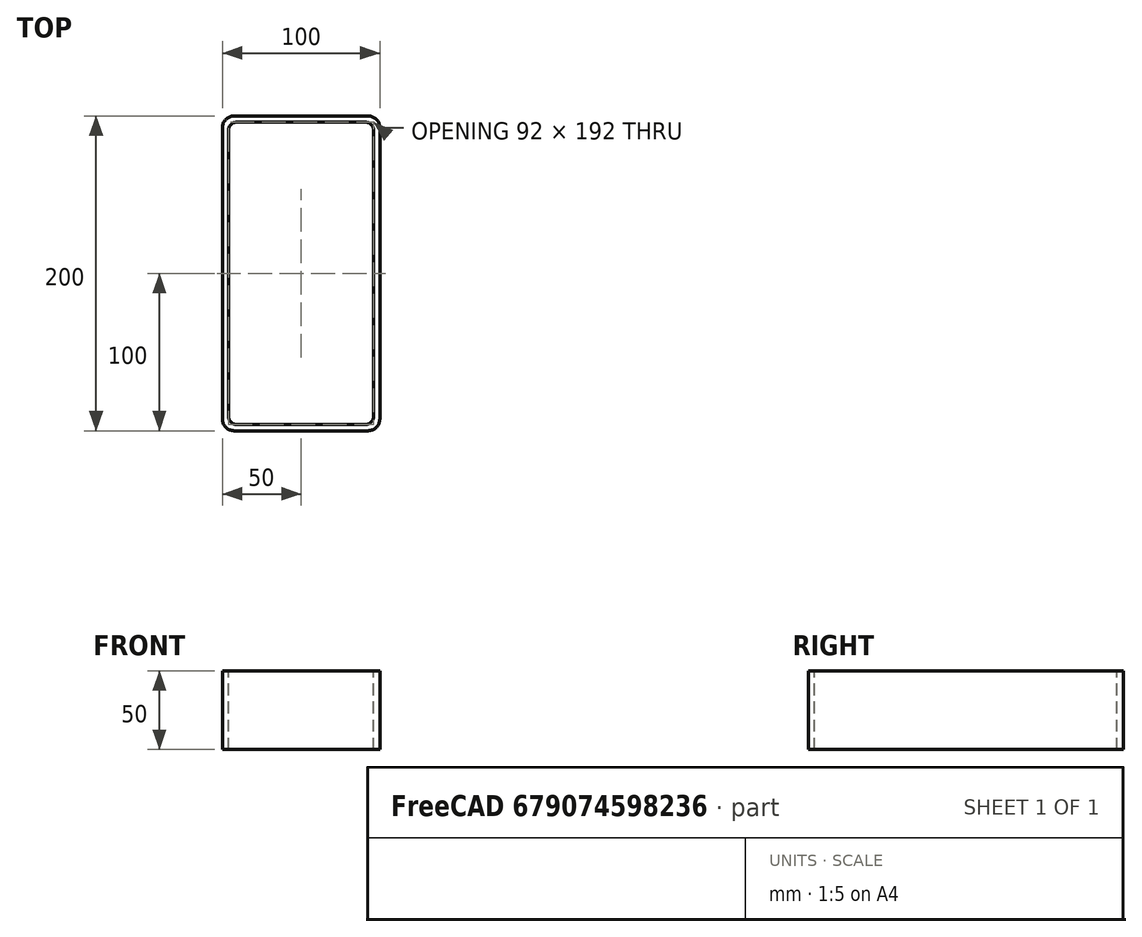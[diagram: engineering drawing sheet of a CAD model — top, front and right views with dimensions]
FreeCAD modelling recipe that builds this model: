
FCSTD DOCUMENT  (FreeCAD 0.15R4671 (Git))
Label: Rectangular hollow section 200x100x4 EN10219 S235JRH
License: All rights reserved
LicenseURL: http://en.wikipedia.org/wiki/All_rights_reserved
objects: Sketcher::SketchObject×1, Part::Extrusion×1
note: 2 computed .brp shape members not serialized (recipe doc carries the construction recipe); baked Part::Feature solids carry a one-line shape summary decoded from their .brp

FEATURE [Sketcher::SketchObject] Sketch
  sketch-geometry (16):
    g0: LineSegment StartX=-41 StartY=96 StartZ=0 EndX=41 EndY=96 EndZ=0
    g1: LineSegment StartX=46 StartY=91 StartZ=0 EndX=46 EndY=-91 EndZ=0
    g2: LineSegment StartX=41 StartY=-96 StartZ=0 EndX=-41 EndY=-96 EndZ=0
    g3: LineSegment StartX=-46 StartY=-91 StartZ=0 EndX=-46 EndY=91 EndZ=0
    g4: LineSegment StartX=-42.5 StartY=100 StartZ=0 EndX=42.5 EndY=100 EndZ=0
    g5: LineSegment StartX=50 StartY=92.5 StartZ=0 EndX=50 EndY=-92.5 EndZ=0
    g6: LineSegment StartX=42.5 StartY=-100 StartZ=0 EndX=-42.5 EndY=-100 EndZ=0
    g7: LineSegment StartX=-50 StartY=-92.5 StartZ=0 EndX=-50 EndY=92.5 EndZ=0
    g8: ArcOfCircle CenterX=-41 CenterY=91 CenterZ=0 NormalX=0 NormalY=0 NormalZ=1 Radius=5 StartAngle=1.5708 EndAngle=3.14159
    g9: ArcOfCircle CenterX=41 CenterY=91 CenterZ=0 NormalX=0 NormalY=0 NormalZ=1 Radius=5 StartAngle=0 EndAngle=1.5708
    g10: ArcOfCircle CenterX=41 CenterY=-91 CenterZ=0 NormalX=0 NormalY=0 NormalZ=1 Radius=5 StartAngle=4.71239 EndAngle=6.28319
    g11: ArcOfCircle CenterX=-41 CenterY=-91 CenterZ=0 NormalX=0 NormalY=0 NormalZ=1 Radius=5 StartAngle=3.14159 EndAngle=4.71239
    g12: ArcOfCircle CenterX=42.5 CenterY=92.5 CenterZ=0 NormalX=0 NormalY=0 NormalZ=1 Radius=7.5 StartAngle=0 EndAngle=1.5708
    g13: ArcOfCircle CenterX=42.5 CenterY=-92.5 CenterZ=0 NormalX=0 NormalY=0 NormalZ=1 Radius=7.5 StartAngle=4.71239 EndAngle=6.28319
    g14: ArcOfCircle CenterX=-42.5 CenterY=-92.5 CenterZ=0 NormalX=0 NormalY=0 NormalZ=1 Radius=7.5 StartAngle=3.14159 EndAngle=4.71239
    g15: ArcOfCircle CenterX=-42.5 CenterY=92.5 CenterZ=0 NormalX=0 NormalY=0 NormalZ=1 Radius=7.5 StartAngle=1.5708 EndAngle=3.14159
  constraints (36):
    c: Horizontal(g2)
    c: Vertical(g3)
    c: Horizontal(g6)
    c: Vertical(g7)
    c: Tangent(g3,g8) = 1.5708
    c: Tangent(g0,g8) = 1.5708
    c: Tangent(g0,g9) = 1.5708
    c: Tangent(g1,g9) = 1.5708
    c: Tangent(g1,g10) = 1.5708
    c: Tangent(g2,g10) = 1.5708
    c: Tangent(g2,g11) = 1.5708
    c: Tangent(g3,g11) = 1.5708
    c: Tangent(g4,g12) = 1.5708
    c: Tangent(g5,g12) = 1.5708
    c: Tangent(g5,g13) = 1.5708
    c: Tangent(g6,g13) = 1.5708
    c: Tangent(g6,g14) = 1.5708
    c: Tangent(g7,g14) = 1.5708
    c: Tangent(g7,g15) = 1.5708
    c: Tangent(g4,g15) = 1.5708
    c: Equal(g9,g8)
    c: Equal(g9,g11)
    c: Equal(g9,g10)
    c: Equal(g12,g15)
    c: Equal(g12,g14)
    c: Equal(g12,g13)
    c: Symmetric(g4,g6,g-1)
    c: Symmetric(g7,g5,g-2)
    c: DistanceY(g4,g6) = -200
    c: DistanceX(g7,g5) = 100
    c: Symmetric(g3,g1,g-2)
    c: Symmetric(g0,g2,g-1)
    c: DistanceY(g0,g4) = 4
    c: DistanceX(g5,g1) = -4
    c: Radius(g9) = 5
    c: Radius(g12) = 7.5
FEATURE [Part::Extrusion] Extrude  label="Rectangular hollow section 200x100x4 EN10219 S235JRH"
  Base = -> Sketch
  Dir = (0,0,50)
  Solid = true
